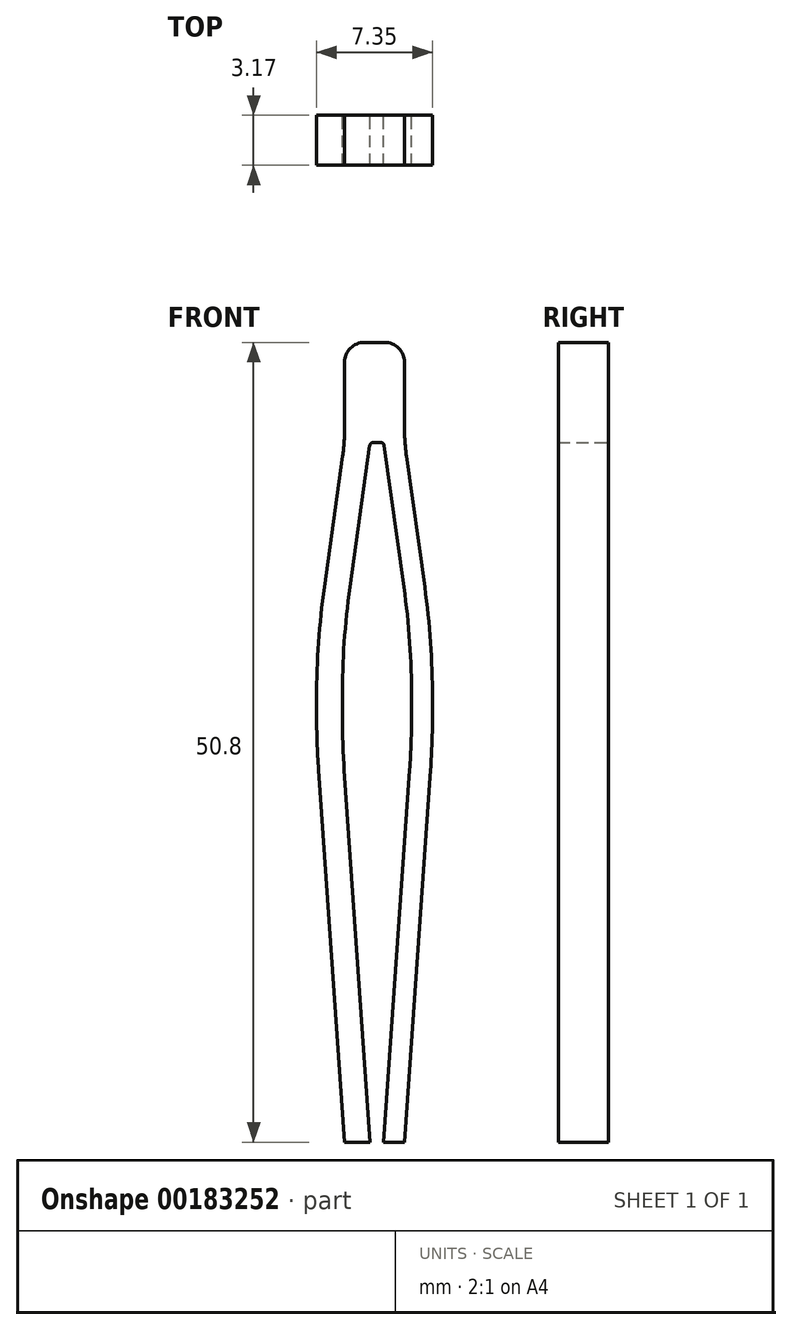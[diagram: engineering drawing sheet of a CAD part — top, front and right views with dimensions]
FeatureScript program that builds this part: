
annotation { "Feature Type Name" : "Feature", "Feature Type Description" : "" }
export const myFeature = defineFeature(function(context is Context, id is Id, definition is map)
    precondition{}
    {
        {
            var Q0;
            Q0=qCreatedBy(makeId("Front.planeOp"),FACE);
            var sketch = newSketch(context, id + "F0", { "sketchPlane" : qUnion([Q0])});
            skLineSegment(sketch, "E0", {"start": v(-3.81, 32.05) * mm, "end": v(0, 32.05) * mm});
            skLineSegment(sketch, "E1", {"start": v(0, 32.05) * mm, "end": v(0, 25.7) * mm});
            skLineSegment(sketch, "E2", {"start": v(0, 25.7) * mm, "end": v(1.77, 13) * mm});
            skLineSegment(sketch, "E3", {"start": v(1.77, 13) * mm, "end": v(1.77, 6.65) * mm});
            skLineSegment(sketch, "E4", {"start": v(1.77, 6.65) * mm, "end": v(0, -18.75) * mm});
            skLineSegment(sketch, "E5", {"start": v(0, 25.7) * mm, "end": v(-22.78, 25.7) * mm, "construction": true});
            skLineSegment(sketch, "E6", {"start": v(1.77, 13) * mm, "end": v(-23.58, 13) * mm, "construction": true});
            skLineSegment(sketch, "E7", {"start": v(1.77, 6.65) * mm, "end": v(-23.5, 6.65) * mm, "construction": true});
            skLineSegment(sketch, "E8", {"start": v(0, -18.75) * mm, "end": v(-15.16, -18.75) * mm, "construction": true});
            skLineSegment(sketch, "E9", {"start": v(-3.81, 32.05) * mm, "end": v(-3.81, 25.7) * mm});
            skLineSegment(sketch, "E10", {"start": v(-3.81, 25.7) * mm, "end": v(-5.58, 13) * mm});
            skLineSegment(sketch, "E11", {"start": v(-5.58, 13) * mm, "end": v(-5.58, 6.65) * mm});
            skLineSegment(sketch, "E12", {"start": v(-5.58, 6.65) * mm, "end": v(-3.81, -18.75) * mm});
            skLineSegment(sketch, "E13", {"start": v(-3.81, -18.75) * mm, "end": v(-2.18, -18.75) * mm});
            skLineSegment(sketch, "E14", {"start": v(-2.18, -18.75) * mm, "end": v(-3.95, 6.65) * mm});
            skLineSegment(sketch, "E15", {"start": v(-3.95, 6.65) * mm, "end": v(-3.95, 13) * mm});
            skLineSegment(sketch, "E16", {"start": v(-3.95, 13) * mm, "end": v(-2.18, 25.7) * mm});
            skLineSegment(sketch, "E17", {"start": v(0, -18.75) * mm, "end": v(-1.33, -18.75) * mm});
            skLineSegment(sketch, "E18", {"start": v(-1.33, -18.75) * mm, "end": v(0.45, 6.65) * mm});
            skLineSegment(sketch, "E19", {"start": v(0.45, 6.65) * mm, "end": v(0.45, 13) * mm});
            skLineSegment(sketch, "E20", {"start": v(0.45, 13) * mm, "end": v(-1.33, 25.7) * mm});
            skLineSegment(sketch, "E21", {"start": v(-1.33, 25.7) * mm, "end": v(-2.18, 25.7) * mm});
            skSolve(sketch);
        }
        {
            var Q0;
            Q0=makeQuery(id+"F0.imprint","IMPRINT",FACE,{"disambiguationData":[TD([[makeQuery(id+"F0.imprint","IMPRINT",EDGE,{"derivedFrom":sQuery(id+"F0.wireOp",EDGE,"E0")}),-1.0]])]});
            extrude(context, id + "F1", {"entities" : qUnion([Q0]), "depth" : 3.17 * mm});
        }
        {
            var Q0;
            Q0=makeQuery(id+"F1.opExtrude","SWEPT_EDGE",EDGE,{"disambiguationData":[OSD([sQuery(id+"F0.wireOp",EDGE,"E10"),sQuery(id+"F0.wireOp",EDGE,"E11")])]});
            var Q1;
            Q1=makeQuery(id+"F1.opExtrude","SWEPT_EDGE",EDGE,{"disambiguationData":[OSD([sQuery(id+"F0.wireOp",EDGE,"E11"),sQuery(id+"F0.wireOp",EDGE,"E12")])]});
            var Q2;
            Q2=makeQuery(id+"F1.opExtrude","SWEPT_EDGE",EDGE,{"disambiguationData":[OSD([sQuery(id+"F0.wireOp",EDGE,"E3"),sQuery(id+"F0.wireOp",EDGE,"E4")])]});
            var Q3;
            Q3=makeQuery(id+"F1.opExtrude","SWEPT_EDGE",EDGE,{"disambiguationData":[OSD([sQuery(id+"F0.wireOp",EDGE,"E2"),sQuery(id+"F0.wireOp",EDGE,"E3")])]});
            var Q4;
            Q4=makeQuery(id+"F1.opExtrude","SWEPT_EDGE",EDGE,{"disambiguationData":[OSD([sQuery(id+"F0.wireOp",EDGE,"E15"),sQuery(id+"F0.wireOp",EDGE,"E16")])]});
            var Q5;
            Q5=makeQuery(id+"F1.opExtrude","SWEPT_EDGE",EDGE,{"disambiguationData":[OSD([sQuery(id+"F0.wireOp",EDGE,"E14"),sQuery(id+"F0.wireOp",EDGE,"E15")])]});
            var Q6;
            Q6=makeQuery(id+"F1.opExtrude","SWEPT_EDGE",EDGE,{"disambiguationData":[OSD([sQuery(id+"F0.wireOp",EDGE,"E18"),sQuery(id+"F0.wireOp",EDGE,"E19")])]});
            var Q7;
            Q7=makeQuery(id+"F1.opExtrude","SWEPT_EDGE",EDGE,{"disambiguationData":[OSD([sQuery(id+"F0.wireOp",EDGE,"E19"),sQuery(id+"F0.wireOp",EDGE,"E20")])]});
            fillet(context, id + "F2", {"entities" : qUnion([Q0, Q1, Q2, Q3, Q4, Q5, Q6, Q7]), "radius" : 50.8 * mm, "tangentPropagation" : true, "allowEdgeOverflow" : false});
        }
        {
            var Q0;
            Q0=makeQuery(id+"F1.opExtrude","SWEPT_EDGE",EDGE,{"disambiguationData":[OSD([sQuery(id+"F0.wireOp",EDGE,"E9"),sQuery(id+"F0.wireOp",EDGE,"E10")])]});
            var Q1;
            Q1=makeQuery(id+"F1.opExtrude","SWEPT_EDGE",EDGE,{"disambiguationData":[OSD([sQuery(id+"F0.wireOp",EDGE,"E1"),sQuery(id+"F0.wireOp",EDGE,"E2")])]});
            fillet(context, id + "F3", {"entities" : qUnion([Q0, Q1]), "radius" : 12.7 * mm, "tangentPropagation" : true, "allowEdgeOverflow" : false});
        }
        {
            var Q0;
            Q0=makeQuery(id+"F1.opExtrude","SWEPT_EDGE",EDGE,{"disambiguationData":[OSD([sQuery(id+"F0.wireOp",EDGE,"E16"),sQuery(id+"F0.wireOp",EDGE,"E21")])]});
            var Q1;
            Q1=makeQuery(id+"F1.opExtrude","SWEPT_EDGE",EDGE,{"disambiguationData":[OSD([sQuery(id+"F0.wireOp",EDGE,"E20"),sQuery(id+"F0.wireOp",EDGE,"E21")])]});
            fillet(context, id + "F4", {"entities" : qUnion([Q0, Q1]), "radius" : 0.25 * mm, "tangentPropagation" : true, "allowEdgeOverflow" : false});
        }
        {
            var Q0;
            Q0=makeQuery(id+"F1.opExtrude","SWEPT_EDGE",EDGE,{"disambiguationData":[OSD([sQuery(id+"F0.wireOp",EDGE,"E0"),sQuery(id+"F0.wireOp",EDGE,"E9")])]});
            var Q1;
            Q1=makeQuery(id+"F1.opExtrude","SWEPT_EDGE",EDGE,{"disambiguationData":[OSD([sQuery(id+"F0.wireOp",EDGE,"E0"),sQuery(id+"F0.wireOp",EDGE,"E1")])]});
            fillet(context, id + "F5", {"entities" : qUnion([Q0, Q1]), "radius" : 1.27 * mm, "tangentPropagation" : true, "allowEdgeOverflow" : false});
        }
    });
